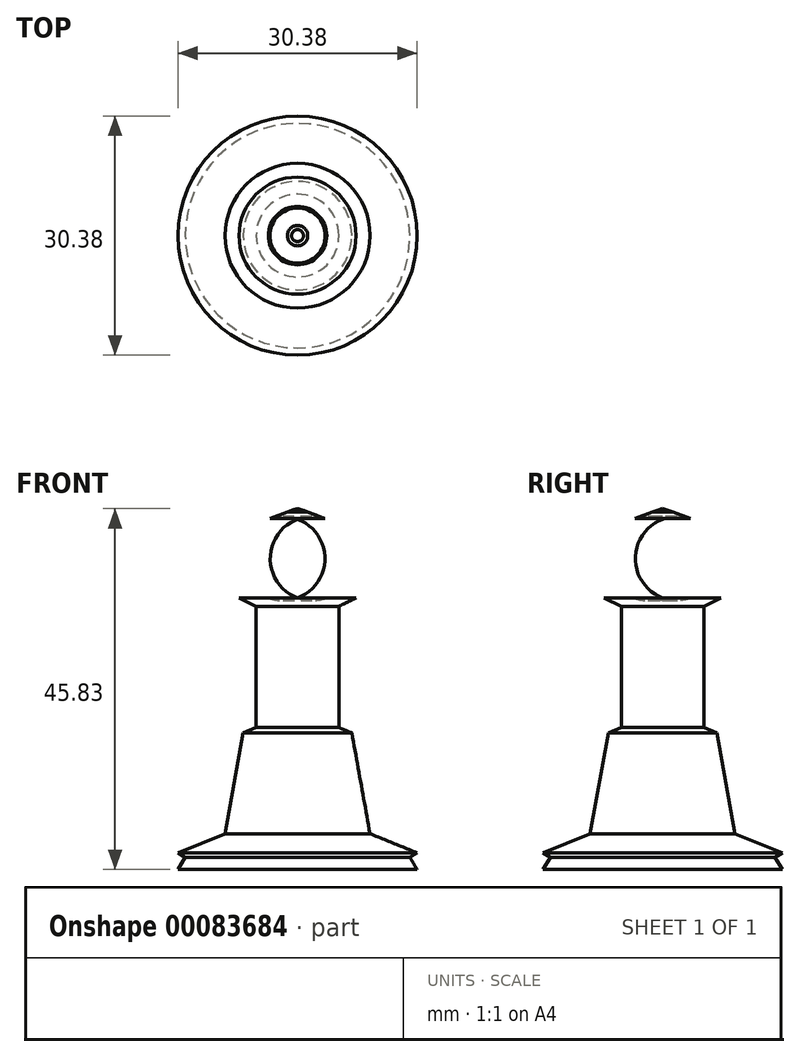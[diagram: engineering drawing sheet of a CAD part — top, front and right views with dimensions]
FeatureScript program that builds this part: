
annotation { "Feature Type Name" : "Feature", "Feature Type Description" : "" }
export const myFeature = defineFeature(function(context is Context, id is Id, definition is map)
    precondition{}
    {
        {
            var Q0;
            Q0=qCreatedBy(makeId("Front.planeOp"),FACE);
            var sketch = newSketch(context, id + "F0", { "sketchPlane" : qUnion([Q0])});
            skLineSegment(sketch, "E0", {"start": v(0, -38.44) * mm, "end": v(15.2, -38.44) * mm});
            skLineSegment(sketch, "E1", {"start": v(15.2, -38.44) * mm, "end": v(14.26, -36.9) * mm});
            skLineSegment(sketch, "E2", {"start": v(14.26, -36.9) * mm, "end": v(15.2, -36.34) * mm});
            skLineSegment(sketch, "E3", {"start": v(15.2, -36.34) * mm, "end": v(9.2, -33.9) * mm});
            skLineSegment(sketch, "E4", {"start": v(9.2, -33.9) * mm, "end": v(6.9, -21.1) * mm});
            skLineSegment(sketch, "E5", {"start": v(6.9, -21.1) * mm, "end": v(5.26, -20.42) * mm});
            skLineSegment(sketch, "E6", {"start": v(5.26, -20.42) * mm, "end": v(5.26, -5) * mm});
            skLineSegment(sketch, "E7", {"start": v(5.26, -5) * mm, "end": v(7.43, -3.95) * mm});
            skLineSegment(sketch, "E8", {"start": v(7.43, -3.95) * mm, "end": v(0, -3.95) * mm});
            skLineSegment(sketch, "E9", {"start": v(0, -3.95) * mm, "end": v(0, -38.44) * mm});
            skArc(sketch, "E10", {"start": v(3.72, -3.95) * mm, "mid": v(6.86, 2.9) * mm, "end": v(0, 6.05) * mm});
            skLineSegment(sketch, "E11", {"start": v(3.5, 6.13) * mm, "end": v(1.3, 6.97) * mm});
            skLineSegment(sketch, "E12", {"start": v(1.3, 6.97) * mm, "end": v(0.75, 7.2) * mm});
            skLineSegment(sketch, "E13", {"start": v(0.75, 7.2) * mm, "end": v(0, 7.39) * mm});
            skLineSegment(sketch, "E14", {"start": v(0, 7.39) * mm, "end": v(0, 6.05) * mm});
            skLineSegment(sketch, "E15", {"start": v(0, -3.95) * mm, "end": v(0, 6.05) * mm});
            skSolve(sketch);
        }
        {
            var Q0;
            {var subQ0=sQuery(id+"F0.wireOp",EDGE,"E15");Q0=makeQuery(id+"F0.imprint","IMPRINT",FACE,{"disambiguationData":[TD([[makeQuery(id+"F0.imprint","IMPRINT",EDGE,{"derivedFrom":subQ0}),-1.0]])]});}
            var Q1;
            {var subQ0=sQuery(id+"F0.wireOp",EDGE,"E11");Q1=makeQuery(id+"F0.imprint","IMPRINT",FACE,{"disambiguationData":[TD([[makeQuery(id+"F0.imprint","IMPRINT",EDGE,{"derivedFrom":subQ0}),1.0]])]});}
            var Q2;
            Q2=makeQuery(id+"F0.imprint","IMPRINT",FACE,{"disambiguationData":[TD([[makeQuery(id+"F0.imprint","IMPRINT",EDGE,{"derivedFrom":sQuery(id+"F0.wireOp",EDGE,"E0")}),1.0]])]});
            var Q3;
            Q3=sQuery(id+"F0.wireOp",EDGE,"E9");
            revolve(context, id + "F1", {"entities" : qUnion([Q0, Q1, Q2]), "axis" : qUnion([Q3]), "revolveType" : RevolveType.FULL});
        }
    });
